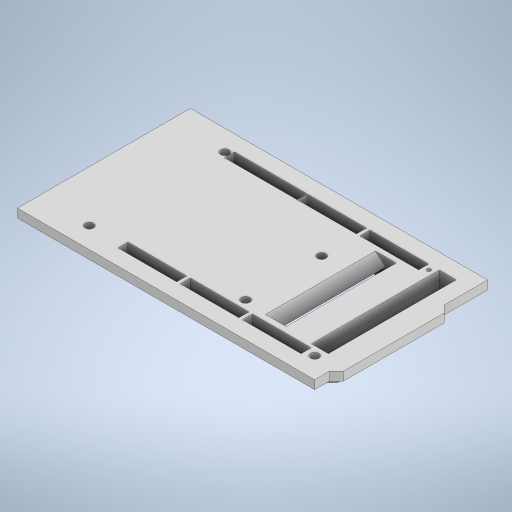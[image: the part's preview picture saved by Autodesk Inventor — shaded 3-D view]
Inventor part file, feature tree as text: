
AUTODESK INVENTOR PART (.ipt)
format: ipt  version: 2024 (Build 280153000, 153)  size: 728,064 bytes
history: native  units: in
note: dims shown in document units (in); Inventor stores cm internally (conversion verified against a paired STEP export)
features: extrude x12, sketch x12, projected_geometry x6, mirror x1
ambient origin geometry x8: Origin, YZ Plane, XZ Plane, XY Plane, X Axis, Y Axis, Z Axis, Center Point
bodies: Solid1 (feature_tree)
feature tree (31):
  extrude  "Extrusion1"  Depth=0.125in
  extrude  "Extrusion5"  Depth=0.25in TaperAngle=0.0deg
  extrude  "Extrusion6"  Depth=0.69in
  extrude  "Extrusion7"  Depth=0.0526in
  extrude  "Extrusion8"  Depth=0.06in
  mirror  "Mirror1"
  extrude  "Extrusion9"  Depth=0.1in
  extrude  "Extrusion10"  Depth=1.05in
  extrude  "Extrusion11"  Depth=0.0526in
  extrude  "Extrusion12"  Depth=0.1in
  extrude  "Extrusion13"  Depth=0.1in
  extrude  "Extrusion14"  Depth=0.2in
  extrude  "Extrusion15"  Depth=0.2in
  sketch  "Sketch12"  dims[d194=0.4959in d195=0.25in d196=0.0in]
  projected_geometry  "Projected Loop2"
  sketch  "Sketch13"  dims[d236=0.2in d237=0.69in]
  sketch  "Sketch14"  dims[d238=0.0526in d239=1.0in]
  sketch  "Sketch15"  dims[d240=0.0949in d241=0.06in]
  projected_geometry  "Projected Loop3"
  sketch  "Sketch16"  dims[d242=0.8in d243=0.1in]
  projected_geometry  "Projected Loop4"
  sketch  "Sketch17"  dims[d244=0.8in d245=1.05in]
  sketch  "Sketch18"  dims[d246=0.0526in d247=0.8in]
  sketch  "Sketch19"  dims[d248=0.0949in d249=0.1in]
  projected_geometry  "Projected Loop5"
  sketch  "Sketch20"  dims[d250=0.0526in d251=0.8in d252=0.0949in d253=0.1in d254=0.8in]
  projected_geometry  "Projected Loop6"
  sketch  "Sketch21"  dims[d255=0.0026in d256=0.1026in d257=0.1949in d258=1.8in d259=0.25in d260=0.0in d261=0.25in d262=0.0in d263=1.0in d264=0.0in d265=0.025in d266=0.025in d267=0.025in d268=0.025in d269=0.025in d270=0.025in d271=0.025in d272=0.025in d273=1.0in d274=0.0in d275=0.0591in d276=0.0in d277=0.0in d278=0.4in d279=0.3in d280=0.2749in d281=1.0in d282=0.0in d283=0.25in d284=0.0in d285=0.0in d286=0.0in d287=0.125in d288=0.125in d289=0.125in d290=0.125in d291=0.125in d292=0.0in d293=0.2in d294=0.0in]
  projected_geometry  "Projected Loop7"
  sketch  "Sketch3"  dims[d74=2.1in d75=0.125in d76=0.075in d77=0.3543in d78=0.3661in d79=0.25in d80=0.474in d81=3.9in d82=3.9in d83=0.5382in d84=0.1in d85=0.6in d86=0.1in d87=0.35in d88=0.1in d89=0.1in d90=0.1in d91=0.7in d92=1.3in d93=1.3in d94=0.3in d95=0.51in d96=0.1in d97=0.1in d98=0.1in d99=0.1in d100=0.1in d101=0.125in d102=0.125in d103=0.125in d104=0.125in d105=0.125in d106=0.125in d107=0.2in d108=0.125in d109=0.2in d110=0.125in]
  sketch  "Sketch5"  dims[d148=2.1in d149=0.125in d150=0.075in d151=0.3543in d152=0.3661in d153=0.25in d154=0.474in d155=3.9in d156=3.9in d157=0.5382in d158=0.1in d159=0.6in d160=0.1in d161=0.35in d162=0.1in d163=0.1in d164=0.1in d165=0.7in d166=1.3in d167=1.3in d168=0.3in d169=0.51in d170=0.1in d171=0.1in d172=0.1in d173=0.1in d174=0.1in d175=0.125in d176=0.125in d177=0.125in d178=0.125in d179=0.125in d180=0.125in d181=0.2in d182=0.125in d183=0.2in d184=0.125in d185=0.125in d186=0.0in d193=0.3996in]
